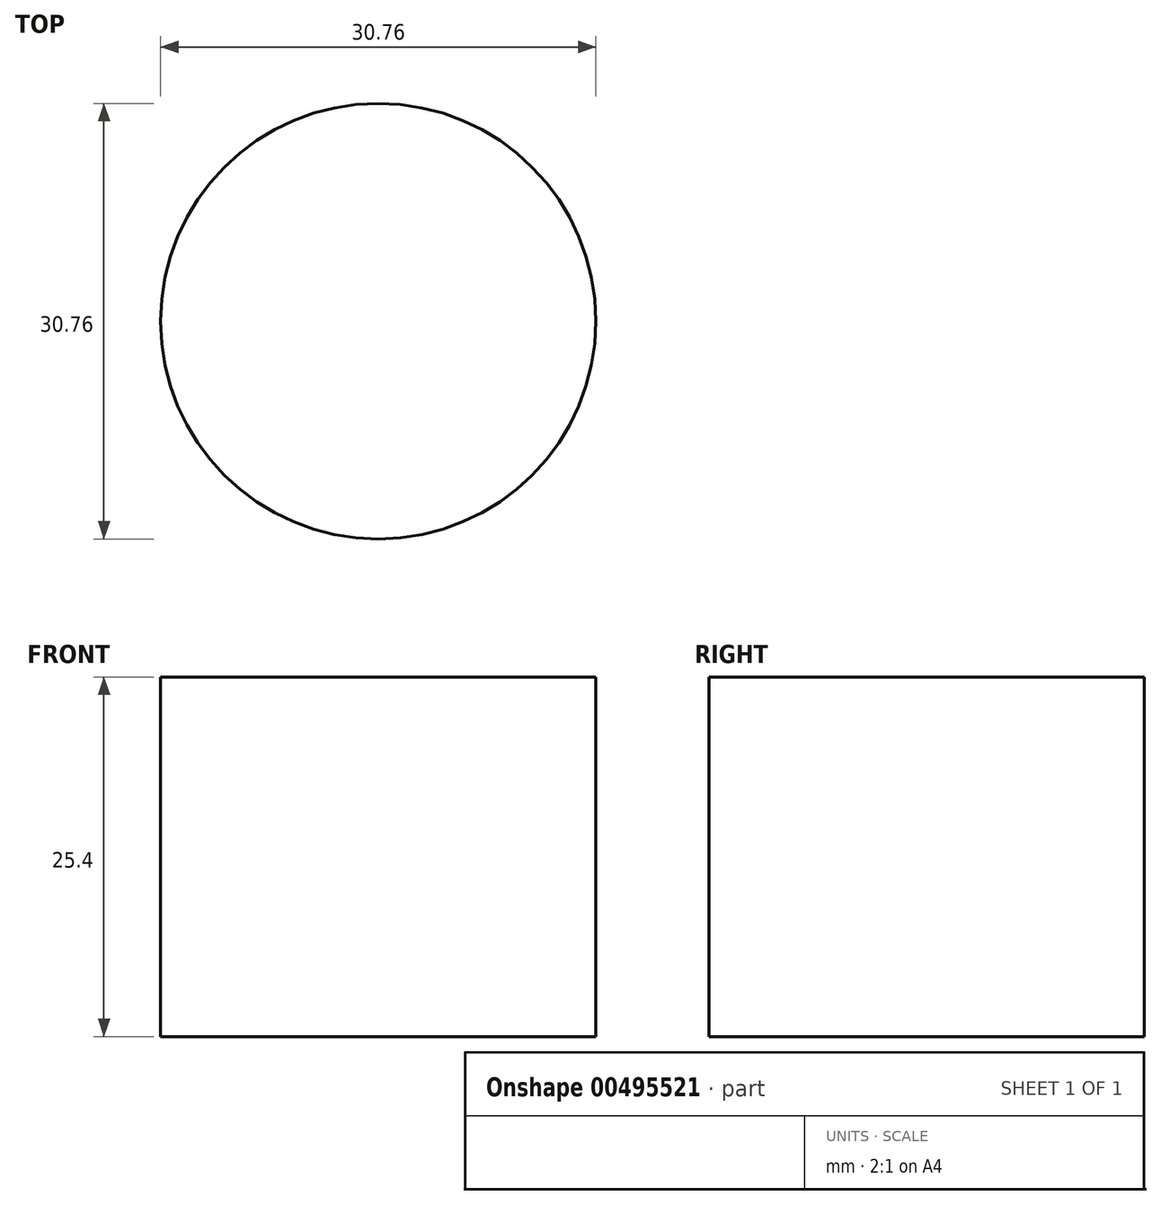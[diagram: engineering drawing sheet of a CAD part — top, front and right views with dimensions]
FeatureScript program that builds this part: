
annotation { "Feature Type Name" : "Feature", "Feature Type Description" : "" }
export const myFeature = defineFeature(function(context is Context, id is Id, definition is map)
    precondition{}
    {
        {
            var Q0;
            Q0=qCreatedBy(makeId("Top.planeOp"),FACE);
            var sketch = newSketch(context, id + "F0", { "sketchPlane" : qUnion([Q0])});
            skCircle(sketch, "E0", {"center": v(0, 0) * mm, "radius": 15.38 * mm});
            skSolve(sketch);
        }
        {
            var Q0;
            Q0 = qSketchRegion(id + "F0", true);
            extrude(context, id + "F1", {"entities" : qUnion([Q0]), "depth" : 25.4 * mm});
        }
    });
